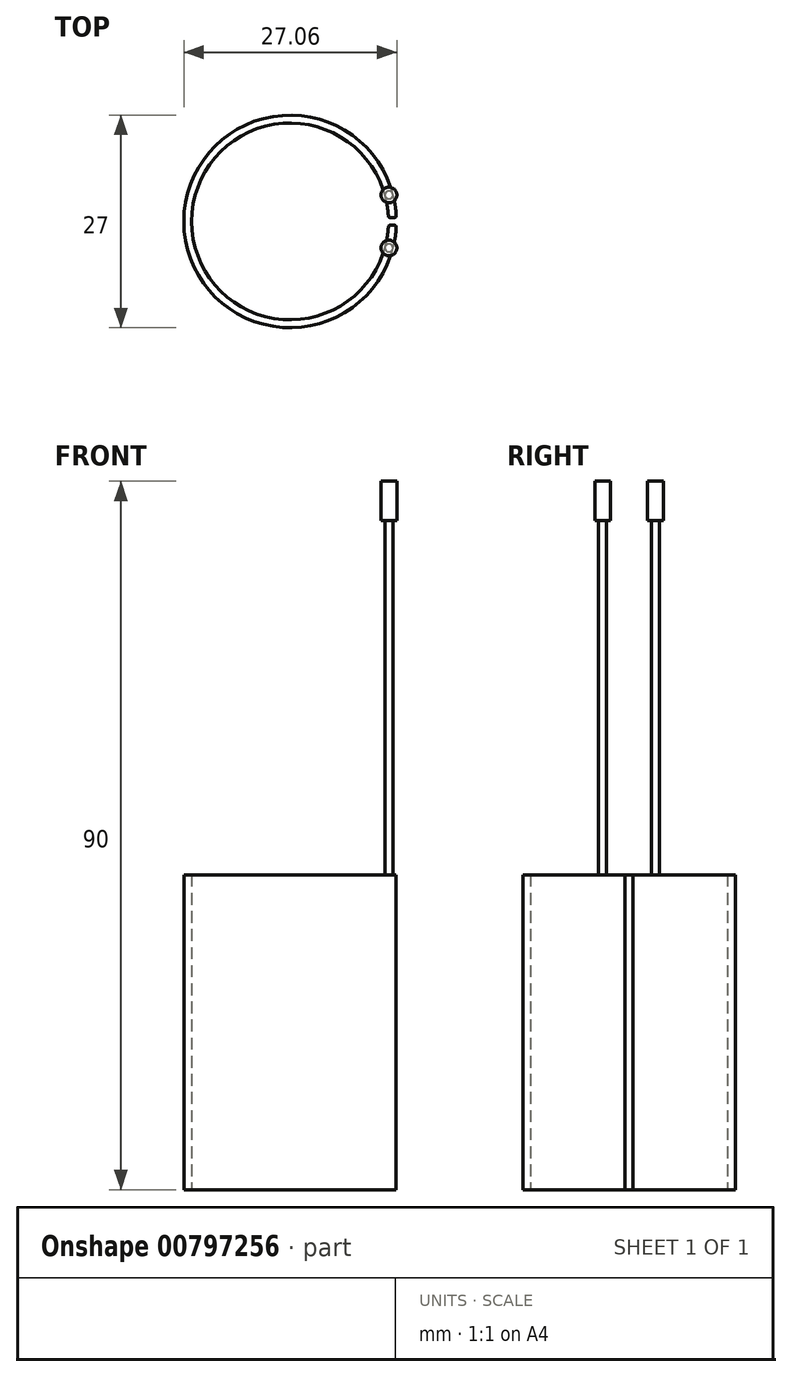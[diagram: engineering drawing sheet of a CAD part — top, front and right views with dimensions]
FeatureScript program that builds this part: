
annotation { "Feature Type Name" : "Feature", "Feature Type Description" : "" }
export const myFeature = defineFeature(function(context is Context, id is Id, definition is map)
    precondition{}
    {
        {
            var Q0;
            Q0=qCreatedBy(makeId("Top.planeOp"),FACE);
            var sketch = newSketch(context, id + "F0", { "sketchPlane" : qUnion([Q0])});
            skArc(sketch, "E0", {"start": v(12.49, 0.5) * mm, "mid": v(-12.5, 0) * mm, "end": v(12.49, -0.5) * mm});
            skArc(sketch, "E1", {"start": v(13.5, 0.5) * mm, "mid": v(-13.5, 0) * mm, "end": v(13.5, -0.5) * mm});
            skLineSegment(sketch, "E2", {"start": v(0, 0) * mm, "end": v(13.5, 0) * mm, "construction": true});
            skLineSegment(sketch, "E3.1.0", {"start": v(0, 0) * mm, "end": v(0, 13.5) * mm, "construction": true});
            skLineSegment(sketch, "E3.2.0", {"start": v(0, 0) * mm, "end": v(-13.5, 0) * mm, "construction": true});
            skLineSegment(sketch, "E3.3.0", {"start": v(0, 0) * mm, "end": v(0, -13.5) * mm, "construction": true});
            skLineSegment(sketch, "E4", {"start": v(12.49, 0.5) * mm, "end": v(13.5, 0.5) * mm});
            skLineSegment(sketch, "E5.MirrorCS", {"start": v(12.49, -0.5) * mm, "end": v(13.5, -0.5) * mm});
            skPoint(sketch, "E6.orphan", {"position": v(0, -0.5) * mm});
            skPoint(sketch, "E7.orphan", {"position": v(0, 0.5) * mm});
            skPoint(sketch, "E8.orphan", {"position": v(15.65, -0.5) * mm});
            skPoint(sketch, "E9.orphan", {"position": v(15.65, 0.5) * mm});
            skSolve(sketch);
        }
        {
            var Q0;
            Q0=makeQuery(id+"F0.imprint","IMPRINT",FACE,{"disambiguationData":[TD([[makeQuery(id+"F0.imprint","IMPRINT",EDGE,{"derivedFrom":sQuery(id+"F0.wireOp",EDGE,"E0")}),-1.0]])]});
            extrude(context, id + "F1", {"entities" : qUnion([Q0]), "depth" : 40 * mm, "offsetDistance" : 25 * mm});
        }
        {
            var Q0;
            Q0=makeQuery(id+"F1.opExtrude","SWEPT_EDGE",EDGE,{"disambiguationData":[OSD([sQuery(id+"F0.wireOp",EDGE,"E1"),sQuery(id+"F0.wireOp",EDGE,"E4")])]});
            var Q1;
            Q1=makeQuery(id+"F1.opExtrude","SWEPT_EDGE",EDGE,{"disambiguationData":[OSD([sQuery(id+"F0.wireOp",EDGE,"E0"),sQuery(id+"F0.wireOp",EDGE,"E4")])]});
            var Q2;
            Q2=makeQuery(id+"F1.opExtrude","SWEPT_EDGE",EDGE,{"disambiguationData":[OSD([sQuery(id+"F0.wireOp",EDGE,"E0"),sQuery(id+"F0.wireOp",EDGE,"E5.MirrorCS")])]});
            var Q3;
            Q3=makeQuery(id+"F1.opExtrude","SWEPT_EDGE",EDGE,{"disambiguationData":[OSD([sQuery(id+"F0.wireOp",EDGE,"E1"),sQuery(id+"F0.wireOp",EDGE,"E5.MirrorCS")])]});
            fillet(context, id + "F2", {"entities" : qUnion([Q0, Q1, Q2, Q3]), "radius" : 0.2 * mm, "tangentPropagation" : true, "allowEdgeOverflow" : false});
        }
        {
            var Q0;
            Q0=makeQuery(id+"F1.opExtrude","CAP_FACE",FACE,{"disambiguationData":[OSD([sQuery(id+"F0.wireOp",EDGE,"E0"),sQuery(id+"F0.wireOp",EDGE,"E1"),sQuery(id+"F0.wireOp",EDGE,"E4"),sQuery(id+"F0.wireOp",EDGE,"E5.MirrorCS")])],"isStart":false});
            var sketch = newSketch(context, id + "F3", { "sketchPlane" : qUnion([Q0])});
            skCircle(sketch, "E10", {"center": v(0, 0) * mm, "radius": 12.5 * mm, "construction": true});
            skPoint(sketch, "E10.first.point", {"position": v(1.8, -12.37) * mm});
            skPoint(sketch, "E10.second.point", {"position": v(-3.72, -11.93) * mm});
            skPoint(sketch, "E10.third.point", {"position": v(12.1, -3.12) * mm});
            skCircle(sketch, "E11", {"center": v(0, 0) * mm, "radius": 13 * mm, "construction": true});
            skLineSegment(sketch, "E12", {"start": v(0, 0) * mm, "end": v(12.5, 0) * mm, "construction": true});
            skLineSegment(sketch, "E13", {"start": v(0, 0) * mm, "end": v(14.64, 3.92) * mm, "construction": true});
            skCircle(sketch, "E14", {"center": v(12.56, 3.36) * mm, "radius": 0.5 * mm});
            skLineSegment(sketch, "E15.MirrorCS", {"start": v(0, 0) * mm, "end": v(14.64, -3.92) * mm, "construction": true});
            skCircle(sketch, "E16.MirrorC", {"center": v(12.56, -3.36) * mm, "radius": 0.5 * mm});
            skSolve(sketch);
        }
        {
            var Q0;
            Q0 = qSketchRegion(id + "F3", true);
            extrude(context, id + "F4", {"entities" : qUnion([Q0]), "operationType" : NewBodyOperationType.ADD, "depth" : 50 * mm, "offsetDistance" : 25 * mm});
        }
        {
            var Q0;
            Q0=makeQuery(id+"F4.opExtrude","CAP_FACE",FACE,{"disambiguationData":[OSD([sQuery(id+"F3.wireOp",EDGE,"E16.MirrorC")])],"isStart":false});
            var sketch = newSketch(context, id + "F5", { "sketchPlane" : qUnion([Q0])});
            skCircle(sketch, "E17", {"center": v(12.56, -3.36) * mm, "radius": 1 * mm});
            skSolve(sketch);
        }
        {
            var Q0;
            Q0 = qSketchRegion(id + "F5", true);
            extrude(context, id + "F6", {"entities" : qUnion([Q0]), "operationType" : NewBodyOperationType.ADD, "oppositeDirection" : true, "depth" : 5 * mm, "offsetDistance" : 25 * mm});
        }
        {
            var Q0;
            Q0=makeQuery(id+"F4.opExtrude","CAP_FACE",FACE,{"disambiguationData":[OSD([sQuery(id+"F3.wireOp",EDGE,"E14")])],"isStart":false});
            var sketch = newSketch(context, id + "F7", { "sketchPlane" : qUnion([Q0])});
            skCircle(sketch, "E18", {"center": v(12.56, 3.36) * mm, "radius": 1 * mm});
            skSolve(sketch);
        }
        {
            var Q0;
            Q0 = qSketchRegion(id + "F7", true);
            extrude(context, id + "F8", {"entities" : qUnion([Q0]), "operationType" : NewBodyOperationType.ADD, "oppositeDirection" : true, "depth" : 5 * mm, "offsetDistance" : 25 * mm});
        }
    });
